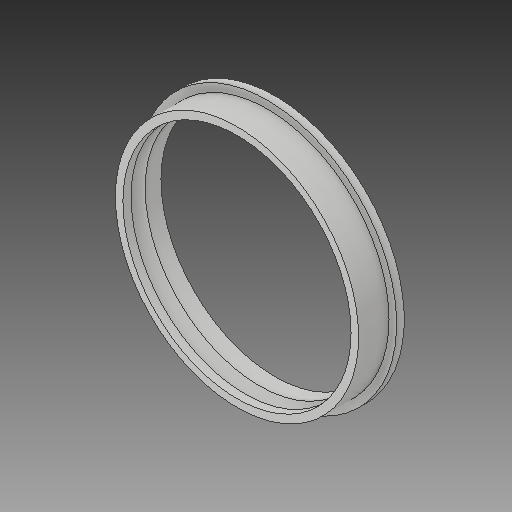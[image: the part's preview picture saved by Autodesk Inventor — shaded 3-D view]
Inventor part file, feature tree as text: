
AUTODESK INVENTOR PART (.ipt)
format: ipt  version: 2018 (Build 220112000, 112)  size: 151,040 bytes
history: native  units: in
note: dims shown in document units (in); Inventor stores cm internally (conversion verified against a paired STEP export)
features: sketch x2, revolve x1, extrude x1, projected_geometry x1
ambient origin geometry x8: Origin, YZ Plane, XZ Plane, XY Plane, X Axis, Y Axis, Z Axis, Center Point
bodies: Solid1 (feature_tree)
feature tree (5):
  revolve  "Revolution1"  [1 undecoded]
  extrude  "Extrusion1"  Depth=0.25in
  sketch  "Sketch1"  dims[d1=1.875in d2=0.124in]
  sketch  "Sketch2"  dims[d3=0.25in d4=0.25in d5=0.0675in d6=0.135in d7=90.0deg d8=0.125in d9=0.125in d10=0.0in]
  projected_geometry  "Projected Loop1"
note: 1 required parameter value undecoded (feature->parameter linkage not recoverable at this tier; creation-order binding heuristic only, values carry confidence <= 0.55)
